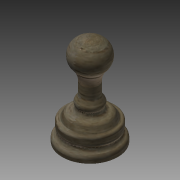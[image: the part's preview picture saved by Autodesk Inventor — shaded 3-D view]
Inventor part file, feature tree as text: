
AUTODESK INVENTOR PART (.ipt)
format: ipt  version: 2015 SP1 (Build 190203100, 203)  size: 204,800 bytes
history: native  units: mm
features: revolve x1, sketch x1
ambient origin geometry x8: Origin, YZ Plane, XZ Plane, XY Plane, X Axis, Y Axis, Z Axis, Center Point
bodies: Solid1 (feature_tree)
feature tree (2):
  revolve  "Revolution1"  [1 undecoded]
  sketch  "Sketch1"  dims[d10=90.0deg d11=2.0mm d13=1.0mm d14=1.0mm d15=2.0mm d16=2.0mm]
note: 1 required parameter value undecoded (feature->parameter linkage not recoverable at this tier; creation-order binding heuristic only, values carry confidence <= 0.55)
